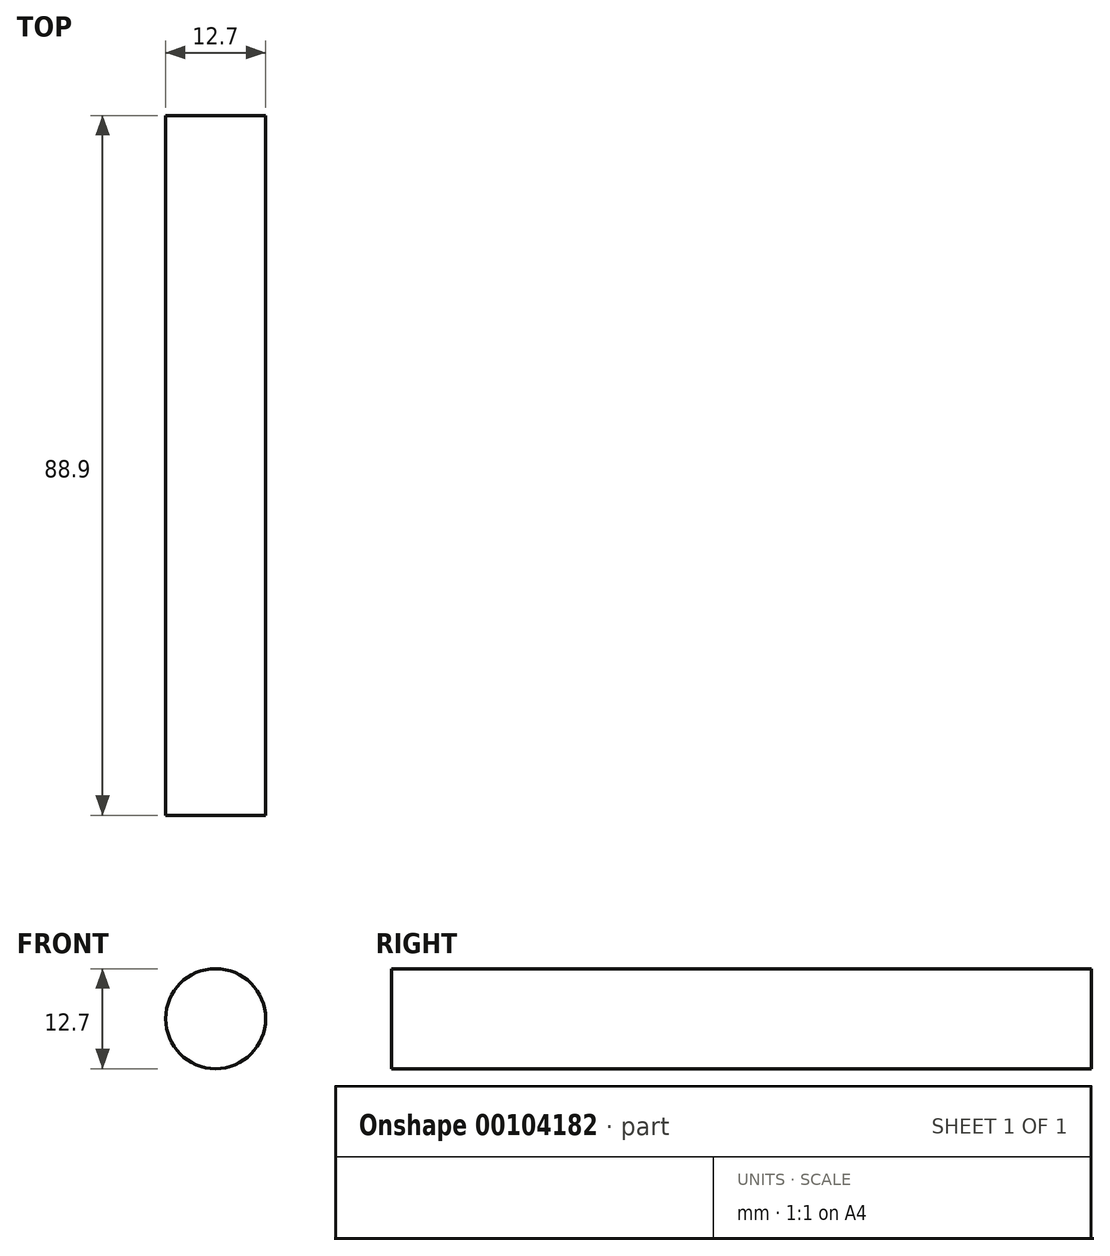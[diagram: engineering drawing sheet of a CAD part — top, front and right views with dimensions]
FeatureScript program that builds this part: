
annotation { "Feature Type Name" : "Feature", "Feature Type Description" : "" }
export const myFeature = defineFeature(function(context is Context, id is Id, definition is map)
    precondition{}
    {
        {
            var Q0;
            Q0=qCreatedBy(makeId("Front.planeOp"),FACE);
            var sketch = newSketch(context, id + "F0", { "sketchPlane" : qUnion([Q0])});
            skCircle(sketch, "E0", {"center": v(-9.33, 20.45) * mm, "radius": 6.35 * mm});
            skSolve(sketch);
        }
        {
            var Q0;
            Q0 = qSketchRegion(id + "F0", true);
            extrude(context, id + "F1", {"entities" : qUnion([Q0]), "depth" : 88.9 * mm});
        }
    });
